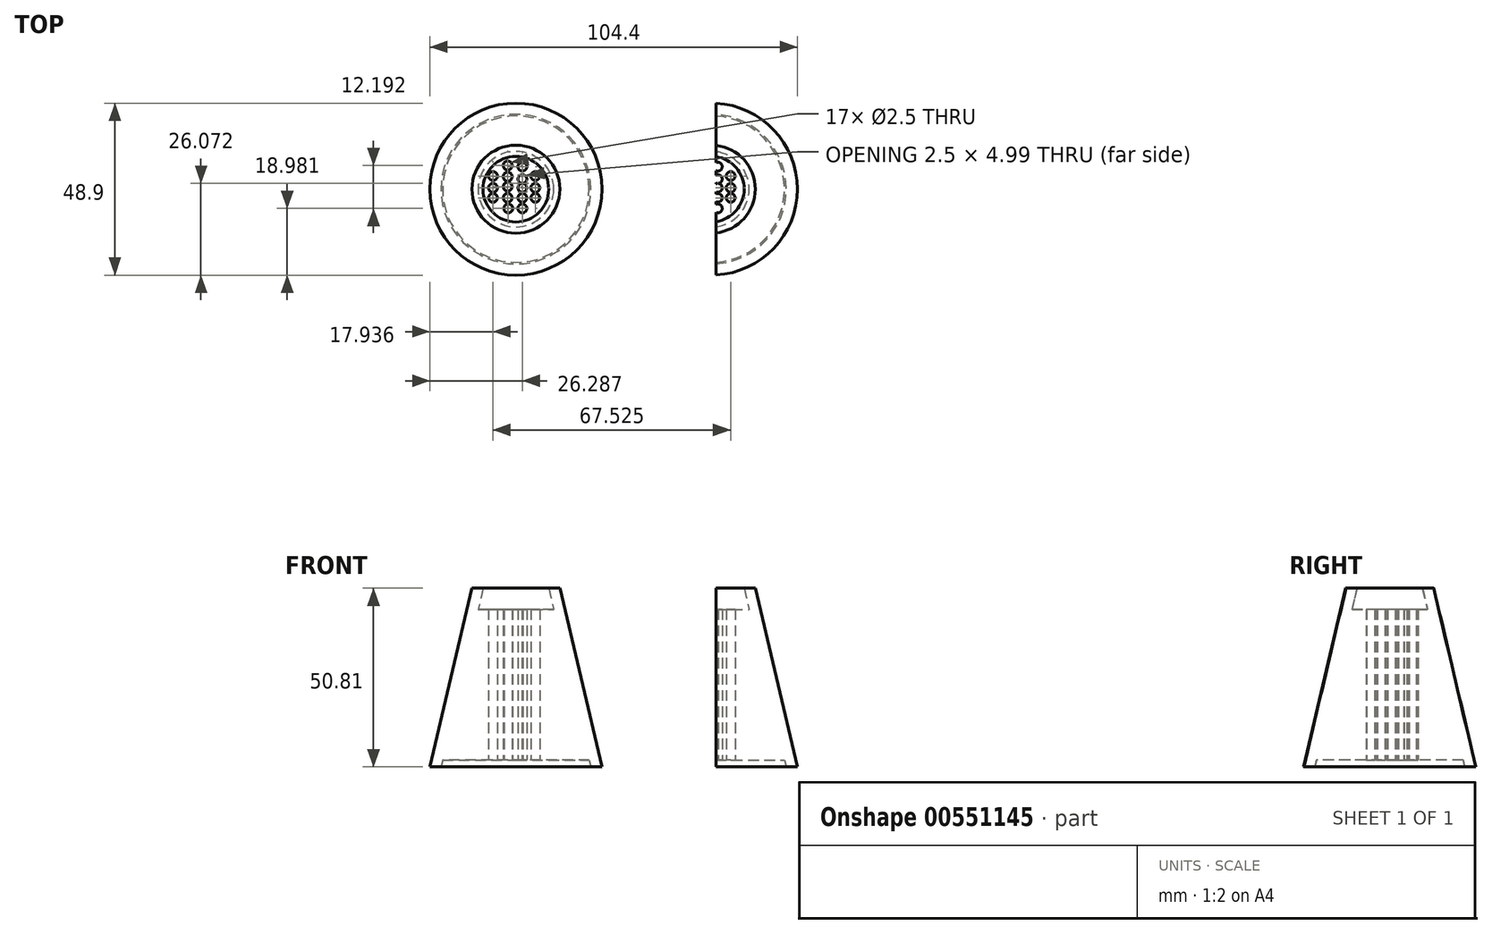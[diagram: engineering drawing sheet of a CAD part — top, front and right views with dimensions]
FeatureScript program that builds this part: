
annotation { "Feature Type Name" : "Feature", "Feature Type Description" : "" }
export const myFeature = defineFeature(function(context is Context, id is Id, definition is map)
    precondition{}
    {
        {
            var Q0;
            Q0=qCreatedBy(makeId("Right.planeOp"),FACE);
            var sketch = newSketch(context, id + "F0", { "sketchPlane" : qUnion([Q0])});
            skLineSegment(sketch, "E0", {"start": v(-38.94, 0) * mm, "end": v(-26.99, 50.81) * mm});
            skLineSegment(sketch, "E1", {"start": v(-26.99, 50.8) * mm, "end": v(-23.81, 50.8) * mm});
            skLineSegment(sketch, "E2", {"start": v(-23.81, 50.8) * mm, "end": v(-35.76, 0) * mm});
            skLineSegment(sketch, "E3", {"start": v(-35.76, 0) * mm, "end": v(-38.94, 0) * mm});
            skLineSegment(sketch, "E4", {"start": v(-35.3, 2) * mm, "end": v(-14.49, 2) * mm});
            skLineSegment(sketch, "E5", {"start": v(-14.49, 2) * mm, "end": v(-14.49, 44.81) * mm});
            skLineSegment(sketch, "E6", {"start": v(-14.49, 44.81) * mm, "end": v(-25.23, 44.81) * mm});
            skSolve(sketch);
        }
        {
            var Q0;
            Q0=makeQuery(id+"F0.imprint","IMPRINT",FACE,{"disambiguationData":[TD([[makeQuery(id+"F0.imprint","IMPRINT",EDGE,{"derivedFrom":sQuery(id+"F0.wireOp",EDGE,"E0")}),-1.0]])]});
            var Q1;
            {var subQ0=sQuery(id+"F0.wireOp",EDGE,"E4");Q1=makeQuery(id+"F0.imprint","IMPRINT",FACE,{"disambiguationData":[TD([[makeQuery(id+"F0.imprint","IMPRINT",EDGE,{"derivedFrom":subQ0}),1.0]])]});}
            var Q2;
            Q2=sQuery(id+"F0.wireOp",EDGE,"E5");
            revolve(context, id + "F1", {"entities" : qUnion([Q0, Q1]), "axis" : qUnion([Q2]), "revolveType" : RevolveType.FULL});
        }
        {
            var Q0;
            Q0=qCreatedBy(makeId("Top.planeOp"),FACE);
            var sketch = newSketch(context, id + "F2", { "sketchPlane" : qUnion([Q0])});
            skPoint(sketch, "E7", {"position": v(-2.34, -7.77) * mm});
            skPoint(sketch, "E8", {"position": v(1.84, -8.1) * mm});
            skPoint(sketch, "E9", {"position": v(-2.34, -10.94) * mm});
            skPoint(sketch, "E10", {"position": v(1.84, -11.62) * mm});
            skPoint(sketch, "E11", {"position": v(-2.34, -13.78) * mm});
            skPoint(sketch, "E12", {"position": v(1.84, -14.11) * mm});
            skPoint(sketch, "E13", {"position": v(-2.34, -16.95) * mm});
            skPoint(sketch, "E14", {"position": v(1.84, -16.95) * mm});
            skPoint(sketch, "E15", {"position": v(5.51, -10.77) * mm});
            skPoint(sketch, "E16", {"position": v(5.51, -14.11) * mm});
            skPoint(sketch, "E17", {"position": v(5.51, -16.95) * mm});
            skPoint(sketch, "E18", {"position": v(-6.51, -16.95) * mm});
            skPoint(sketch, "E19", {"position": v(-6.51, -14.11) * mm});
            skPoint(sketch, "E20", {"position": v(-6.51, -10.77) * mm});
            skPoint(sketch, "E21", {"position": v(-2.16, -19.96) * mm});
            skPoint(sketch, "E22", {"position": v(1.84, -19.96) * mm});
            skSolve(sketch);
        }
        {
            var Q0;
            Q0=sQuery(id+"F2.wireOp",VERTEX,"E20");
            var Q1;
            Q1=sQuery(id+"F2.wireOp",VERTEX,"E19");
            var Q2;
            Q2=sQuery(id+"F2.wireOp",VERTEX,"E18");
            var Q3;
            Q3=sQuery(id+"F2.wireOp",VERTEX,"E13");
            var Q4;
            Q4=sQuery(id+"F2.wireOp",VERTEX,"E21");
            var Q5;
            Q5=sQuery(id+"F2.wireOp",VERTEX,"E22");
            var Q6;
            Q6=sQuery(id+"F2.wireOp",VERTEX,"E14");
            var Q7;
            Q7=sQuery(id+"F2.wireOp",VERTEX,"E12");
            var Q8;
            Q8=sQuery(id+"F2.wireOp",VERTEX,"E11");
            var Q9;
            Q9=sQuery(id+"F2.wireOp",VERTEX,"E9");
            var Q10;
            Q10=sQuery(id+"F2.wireOp",VERTEX,"E7");
            var Q11;
            Q11=sQuery(id+"F2.wireOp",VERTEX,"E8");
            var Q12;
            Q12=sQuery(id+"F2.wireOp",VERTEX,"E10");
            var Q13;
            Q13=sQuery(id+"F2.wireOp",VERTEX,"E15");
            var Q14;
            Q14=sQuery(id+"F2.wireOp",VERTEX,"E16");
            var Q15;
            Q15=sQuery(id+"F2.wireOp",VERTEX,"E17");
            var Q16;
            Q16=makeQuery(id+"F1.opRevolve","SWEPT_BODY",BODY,{"disambiguationData":[OSD([sQuery(id+"F0.wireOp",EDGE,"E0"),sQuery(id+"F0.wireOp",EDGE,"E1"),sQuery(id+"F0.wireOp",EDGE,"E2"),sQuery(id+"F0.wireOp",EDGE,"E3"),sQuery(id+"F0.wireOp",EDGE,"E4"),sQuery(id+"F0.wireOp",EDGE,"E5"),sQuery(id+"F0.wireOp",EDGE,"E6")])]});
            hole(context, id + "F3", {"style" : HoleStyle.SIMPLE, "endStyle" : HoleEndStyle.BLIND, "oppositeDirection" : true, "holeDiameter" : 2.5 * mm, "holeDepth" : 2000 * mm, "isTappedThrough" : true, "tappedDepth" : 12 * mm, "tapClearance" : 3, "locations" : qUnion([Q0, Q1, Q2, Q3, Q4, Q5, Q6, Q7, Q8, Q9, Q10, Q11, Q12, Q13, Q14, Q15]), "scope" : qUnion([Q16])});
        }
        {
            var Q0;
            Q0=makeQuery(id+"F1.opRevolve","SWEPT_BODY",BODY,{"disambiguationData":[OSD([sQuery(id+"F0.wireOp",EDGE,"E0"),sQuery(id+"F0.wireOp",EDGE,"E1"),sQuery(id+"F0.wireOp",EDGE,"E2"),sQuery(id+"F0.wireOp",EDGE,"E3"),sQuery(id+"F0.wireOp",EDGE,"E4"),sQuery(id+"F0.wireOp",EDGE,"E5"),sQuery(id+"F0.wireOp",EDGE,"E6")])]});
            transform(context, id + "F4", {"entities" : qUnion([Q0]), "transformType" : TransformType.TRANSLATION_3D, "dx" : 55.5 * mm, "dy" : 0 * mm, "dz" : 0 * mm, "makeCopy" : true});
        }
        {
            var Q0;
            Q0=qCreatedBy(makeId("Top.planeOp"),FACE);
            var sketch = newSketch(context, id + "F5", { "sketchPlane" : qUnion([Q0])});
            skLineSegment(sketch, "E23", {"start": v(56.8, -44.36) * mm, "end": v(56.8, 18.96) * mm});
            skLineSegment(sketch, "E24", {"start": v(56.8, 18.96) * mm, "end": v(23.05, 18.96) * mm});
            skLineSegment(sketch, "E25", {"start": v(23.05, 18.96) * mm, "end": v(30.12, -44.68) * mm});
            skLineSegment(sketch, "E26", {"start": v(30.12, -44.68) * mm, "end": v(56.8, -44.36) * mm});
            skSolve(sketch);
        }
        {
            var Q0;
            Q0=makeQuery(id+"F5.imprint","IMPRINT",FACE,{"disambiguationData":[TD([[makeQuery(id+"F5.imprint","IMPRINT",EDGE,{"derivedFrom":sQuery(id+"F5.wireOp",EDGE,"E23")}),1.0]])]});
            extrude(context, id + "F6", {"entities" : qUnion([Q0]), "operationType" : NewBodyOperationType.REMOVE, "depth" : 61 * mm, "offsetDistance" : 25 * mm});
        }
    });
